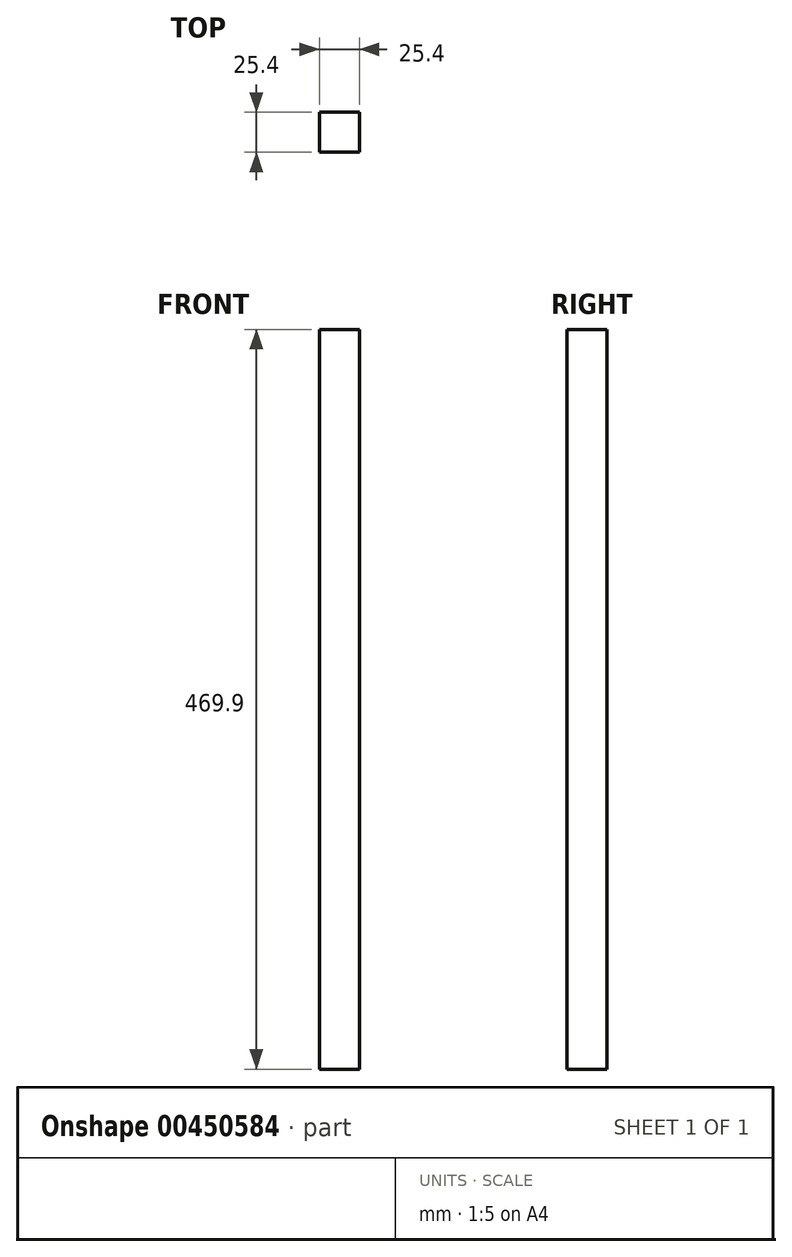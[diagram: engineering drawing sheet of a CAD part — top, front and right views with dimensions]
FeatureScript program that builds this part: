
annotation { "Feature Type Name" : "Feature", "Feature Type Description" : "" }
export const myFeature = defineFeature(function(context is Context, id is Id, definition is map)
    precondition{}
    {
        {
            var Q0;
            Q0=qCreatedBy(makeId("Top.planeOp"),FACE);
            var sketch = newSketch(context, id + "F0", { "sketchPlane" : qUnion([Q0])});
            skLineSegment(sketch, "E0.bottom", {"start": v(12.7, -12.7) * mm, "end": v(-12.7, -12.7) * mm});
            skLineSegment(sketch, "E0.top", {"start": v(12.7, 12.7) * mm, "end": v(-12.7, 12.7) * mm});
            skLineSegment(sketch, "E0.left", {"start": v(12.7, -12.7) * mm, "end": v(12.7, 12.7) * mm});
            skLineSegment(sketch, "E0.right", {"start": v(-12.7, -12.7) * mm, "end": v(-12.7, 12.7) * mm});
            skPoint(sketch, "E0.middle", {"position": v(0, 0) * mm});
            skSolve(sketch);
        }
        {
            var Q0;
            Q0 = qSketchRegion(id + "F0", true);
            extrude(context, id + "F1", {"entities" : qUnion([Q0]), "depth" : 469.9 * mm});
        }
    });
